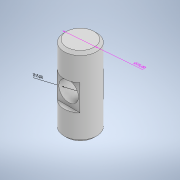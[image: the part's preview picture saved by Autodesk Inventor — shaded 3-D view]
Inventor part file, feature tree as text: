
AUTODESK INVENTOR PART (.ipt)
format: ipt  version: 2021 (Build 250183000, 183)  size: 138,752 bytes
history: native  units: mm
features: other x3, extrude x3, sketch x3, chamfer x1
ambient origin geometry x8: Origin, YZ Plane, XZ Plane, XY Plane, X Axis, Y Axis, Z Axis, Center Point
bodies: Solid1 (feature_tree)
feature tree (10):
  other  "Annotations"
  extrude  "Extrusion1"  Depth=60.0mm TaperAngle=0.0deg
  extrude  "Extrusion2"  Depth=60.0mm
  chamfer  "Chamfer1"  Distance=60.0mm
  extrude  "Extrusion3"  Depth=20.0mm
  sketch  "Sketch1"  dims[d0=25.0mm d1=60.0mm d2=0.0mm]
  sketch  "Sketch2"  dims[d3=30.0mm d4=15.0mm d5=60.0mm d6=0.0mm]
  sketch  "Sketch3"  dims[d17=2.0mm d18=2.0mm d19=45.0deg d20=20.0mm d21=9.0mm d22=20.0mm d23=18.0mm d24=25.0mm d25=0.0mm d11=32.163483mm d12=8.638101mm d13=1.058985mm d14=15.0mm d15=32.262659mm d16=25.0mm d30=0.5mm d31=0.872665mm d32=0.5mm d33=0.872665mm]
  other  "Diameter Dimension 2"
  other  "Diameter Dimension 3"
